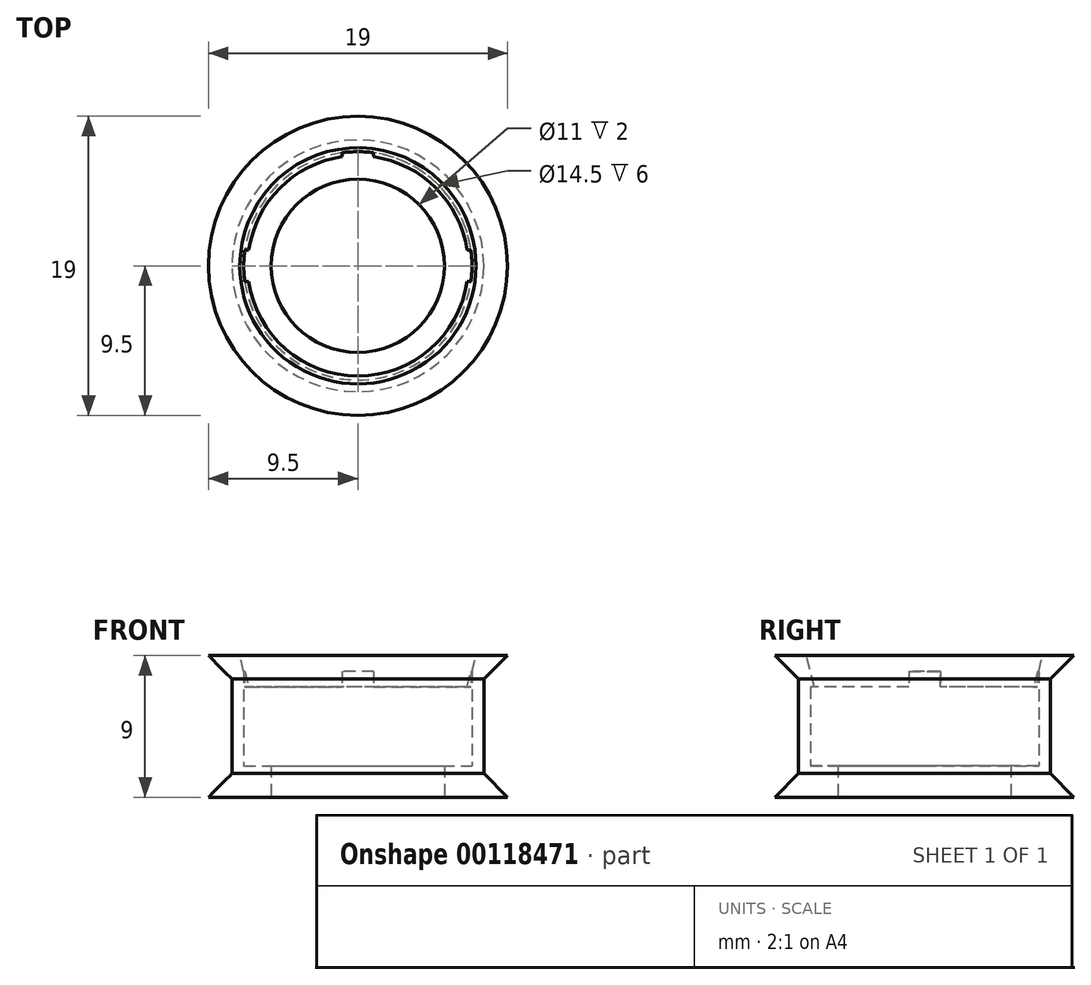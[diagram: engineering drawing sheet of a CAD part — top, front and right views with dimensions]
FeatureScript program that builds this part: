
annotation { "Feature Type Name" : "Feature", "Feature Type Description" : "" }
export const myFeature = defineFeature(function(context is Context, id is Id, definition is map)
    precondition{}
    {
        {
            var Q0;
            Q0=qCreatedBy(makeId("Front.planeOp"),FACE);
            var sketch = newSketch(context, id + "F0", { "sketchPlane" : qUnion([Q0])});
            skLineSegment(sketch, "E0", {"start": v(-5.5, 0) * mm, "end": v(-5.5, 2) * mm});
            skLineSegment(sketch, "E1", {"start": v(-5.5, 2) * mm, "end": v(-7.25, 2) * mm});
            skLineSegment(sketch, "E2", {"start": v(-7.25, 2) * mm, "end": v(-7.25, 7) * mm});
            skLineSegment(sketch, "E3", {"start": v(-7.25, 7) * mm, "end": v(-7, 7) * mm});
            skLineSegment(sketch, "E4", {"start": v(-7, 7) * mm, "end": v(-7.5, 9) * mm});
            skLineSegment(sketch, "E5", {"start": v(-7.5, 9) * mm, "end": v(-9.5, 9) * mm});
            skLineSegment(sketch, "E6", {"start": v(-9.5, 9) * mm, "end": v(-8, 7.5) * mm});
            skLineSegment(sketch, "E7", {"start": v(-8, 7.5) * mm, "end": v(-8, 1.5) * mm});
            skLineSegment(sketch, "E8", {"start": v(-8, 1.5) * mm, "end": v(-9.5, 0) * mm});
            skLineSegment(sketch, "E9", {"start": v(-9.5, 0) * mm, "end": v(-5.5, 0) * mm});
            skLineSegment(sketch, "E10.MirrorCS", {"start": v(5.5, 0) * mm, "end": v(5.5, 2) * mm});
            skLineSegment(sketch, "E11.MirrorCS", {"start": v(5.5, 2) * mm, "end": v(7.25, 2) * mm});
            skLineSegment(sketch, "E12.MirrorCS", {"start": v(7.25, 2) * mm, "end": v(7.25, 7) * mm});
            skLineSegment(sketch, "E13.MirrorCS", {"start": v(7.25, 7) * mm, "end": v(7, 7) * mm});
            skLineSegment(sketch, "E14.MirrorCS", {"start": v(7, 7) * mm, "end": v(7.5, 9) * mm});
            skLineSegment(sketch, "E15.MirrorCS", {"start": v(7.5, 9) * mm, "end": v(9.5, 9) * mm});
            skLineSegment(sketch, "E16.MirrorCS", {"start": v(9.5, 9) * mm, "end": v(8, 7.5) * mm});
            skLineSegment(sketch, "E17.MirrorCS", {"start": v(8, 7.5) * mm, "end": v(8, 1.5) * mm});
            skLineSegment(sketch, "E18.MirrorCS", {"start": v(8, 1.5) * mm, "end": v(9.5, 0) * mm});
            skLineSegment(sketch, "E19.MirrorCS", {"start": v(9.5, 0) * mm, "end": v(5.5, 0) * mm});
            skPoint(sketch, "E20", {"position": v(-8, 4.5) * mm});
            skPoint(sketch, "E21", {"position": v(-7.25, 4.5) * mm});
            skLineSegment(sketch, "E22", {"start": v(0, 0) * mm, "end": v(0, 9) * mm, "construction": true});
            skSolve(sketch);
        }
        {
            var Q0;
            Q0=makeQuery(id+"F0.imprint","IMPRINT",FACE,{"disambiguationData":[TD([[makeQuery(id+"F0.imprint","IMPRINT",EDGE,{"derivedFrom":sQuery(id+"F0.wireOp",EDGE,"E0")}),1.0]])]});
            var Q1;
            Q1=sQuery(id+"F0.wireOp",EDGE,"E22");
            revolve(context, id + "F1", {"entities" : qUnion([Q0]), "axis" : qUnion([Q1]), "revolveType" : RevolveType.FULL});
        }
        {
            var Q0;
            Q0=makeQuery(id+"F1.opRevolve","SWEPT_FACE",FACE,{"disambiguationData":[OSD([sQuery(id+"F0.wireOp",EDGE,"E1")])]});
            var sketch = newSketch(context, id + "F2", { "sketchPlane" : qUnion([Q0])});
            skCircle(sketch, "E23", {"center": v(0, 0) * mm, "radius": 7.25 * mm});
            skLineSegment(sketch, "E24", {"start": v(-7.18, 1) * mm, "end": v(7.18, 1) * mm});
            skLineSegment(sketch, "E25", {"start": v(-1, 7.18) * mm, "end": v(-1, -7.18) * mm});
            skLineSegment(sketch, "E26.MirrorCS", {"start": v(1, 7.18) * mm, "end": v(1, -7.18) * mm});
            skLineSegment(sketch, "E27.MirrorCS", {"start": v(-7.18, -1) * mm, "end": v(7.18, -1) * mm});
            skSolve(sketch);
        }
        {
            var Q0;
            {var subQ0=sQuery(id+"F2.wireOp",EDGE,"E24");var subQ1=sQuery(id+"F2.wireOp",EDGE,"E23");var subQ2=makeQuery(id+"F2.imprint","INTERSECT",VERTEX,{"disambiguationData":[OD(0.0)],"derivedFrom":[subQ1,subQ0]});Q0=makeQuery(id+"F2.imprint","IMPRINT",FACE,{"disambiguationData":[TD([[makeQuery(id+"F2.imprint","IMPRINT",EDGE,{"disambiguationData":[TD([[subQ2,-1.0]])],"derivedFrom":subQ1}),-1.0]])]});}
            var Q1;
            {var subQ0=sQuery(id+"F2.wireOp",EDGE,"E24");var subQ1=sQuery(id+"F2.wireOp",EDGE,"E23");var subQ2=makeQuery(id+"F2.imprint","INTERSECT",VERTEX,{"disambiguationData":[OD(1.0)],"derivedFrom":[subQ1,subQ0]});Q1=makeQuery(id+"F2.imprint","IMPRINT",FACE,{"disambiguationData":[TD([[makeQuery(id+"F2.imprint","IMPRINT",EDGE,{"disambiguationData":[TD([[subQ2,1.0]])],"derivedFrom":subQ1}),-1.0]])]});}
            var Q2;
            {var subQ0=sQuery(id+"F2.wireOp",EDGE,"E26.MirrorCS");var subQ1=sQuery(id+"F2.wireOp",EDGE,"E23");var subQ2=makeQuery(id+"F2.imprint","INTERSECT",VERTEX,{"disambiguationData":[OD(1.0)],"derivedFrom":[subQ1,subQ0]});Q2=makeQuery(id+"F2.imprint","IMPRINT",FACE,{"disambiguationData":[TD([[makeQuery(id+"F2.imprint","IMPRINT",EDGE,{"disambiguationData":[TD([[subQ2,1.0]])],"derivedFrom":subQ1}),-1.0]])]});}
            var Q3;
            {var subQ0=sQuery(id+"F2.wireOp",EDGE,"E25");var subQ1=sQuery(id+"F2.wireOp",EDGE,"E23");var subQ2=makeQuery(id+"F2.imprint","INTERSECT",VERTEX,{"disambiguationData":[OD(1.0)],"derivedFrom":[subQ1,subQ0]});Q3=makeQuery(id+"F2.imprint","IMPRINT",FACE,{"disambiguationData":[TD([[makeQuery(id+"F2.imprint","IMPRINT",EDGE,{"disambiguationData":[TD([[subQ2,-1.0]])],"derivedFrom":subQ1}),-1.0]])]});}
            var Q4;
            Q4=makeQuery(id+"F1.opRevolve","SWEPT_FACE",FACE,{"disambiguationData":[OSD([sQuery(id+"F0.wireOp",EDGE,"E5")])]});
            extrude(context, id + "F3", {"entities" : qUnion([Q0, Q1, Q2, Q3]), "operationType" : NewBodyOperationType.REMOVE, "endBound" : BoundingType.UP_TO_SURFACE, "endBoundEntityFace" : qUnion([Q4]), "depth" : 25 * mm});
        }
    });
